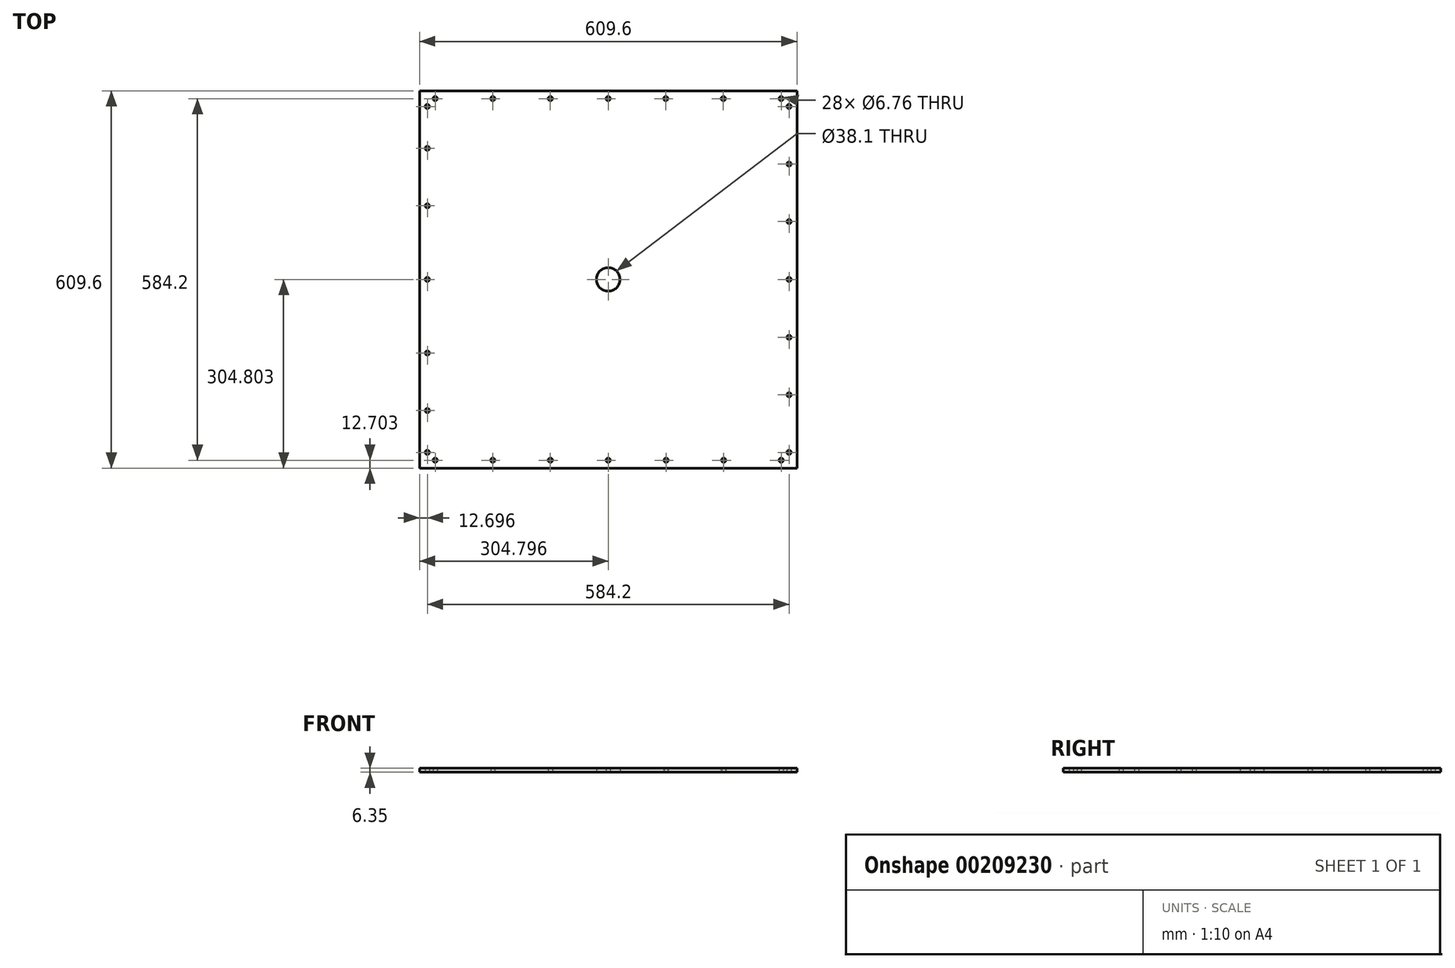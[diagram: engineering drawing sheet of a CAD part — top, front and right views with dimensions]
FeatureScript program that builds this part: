
annotation { "Feature Type Name" : "Feature", "Feature Type Description" : "" }
export const myFeature = defineFeature(function(context is Context, id is Id, definition is map)
    precondition{}
    {
        {
            var Q0;
            Q0=qCreatedBy(makeId("Top.planeOp"),FACE);
            var sketch = newSketch(context, id + "F0", { "sketchPlane" : qUnion([Q0])});
            skLineSegment(sketch, "E0.bottom", {"start": v(-439.06, 399.92) * mm, "end": v(170.54, 399.92) * mm});
            skLineSegment(sketch, "E0.top", {"start": v(-439.06, -209.68) * mm, "end": v(170.54, -209.68) * mm});
            skLineSegment(sketch, "E0.left", {"start": v(-439.06, 399.92) * mm, "end": v(-439.06, -209.68) * mm});
            skLineSegment(sketch, "E0.right", {"start": v(170.54, 399.92) * mm, "end": v(170.54, -209.68) * mm});
            skPoint(sketch, "E1", {"position": v(-439.06, 399.92) * mm});
            skPoint(sketch, "E2", {"position": v(170.54, 399.92) * mm});
            skPoint(sketch, "E3", {"position": v(170.54, -209.68) * mm});
            skPoint(sketch, "E4", {"position": v(-439.06, -209.68) * mm});
            skLineSegment(sketch, "E5", {"start": v(-439.06, 399.92) * mm, "end": v(170.54, -209.68) * mm, "construction": true});
            skLineSegment(sketch, "E6", {"start": v(170.54, 399.92) * mm, "end": v(-439.06, -209.68) * mm, "construction": true});
            skPoint(sketch, "E7", {"position": v(-134.26, 95.12) * mm});
            skCircle(sketch, "E8", {"center": v(-134.26, 95.12) * mm, "radius": 19.05 * mm});
            skPoint(sketch, "E9", {"position": v(-134.26, 399.92) * mm});
            skPoint(sketch, "E10", {"position": v(-426.36, 399.92) * mm});
            skPoint(sketch, "E11", {"position": v(157.84, 399.92) * mm});
            skPoint(sketch, "E12", {"position": v(170.54, 387.22) * mm});
            skPoint(sketch, "E13", {"position": v(-439.06, 387.22) * mm});
            skPoint(sketch, "E14", {"position": v(-439.06, -196.98) * mm});
            skPoint(sketch, "E15", {"position": v(-426.36, -209.68) * mm});
            skPoint(sketch, "E16", {"position": v(157.84, -209.68) * mm});
            skPoint(sketch, "E17", {"position": v(170.54, -196.98) * mm});
            skLineSegment(sketch, "E18", {"start": v(-439.06, 387.22) * mm, "end": v(170.54, 387.22) * mm, "construction": true});
            skLineSegment(sketch, "E19", {"start": v(-439.06, -196.98) * mm, "end": v(170.54, -196.98) * mm, "construction": true});
            skLineSegment(sketch, "E20", {"start": v(-439.06, -196.98) * mm, "end": v(-439.06, -106.24) * mm, "construction": true});
            skLineSegment(sketch, "E21", {"start": v(-426.36, 399.92) * mm, "end": v(-426.36, -209.68) * mm, "construction": true});
            skLineSegment(sketch, "E22", {"start": v(157.84, 399.92) * mm, "end": v(157.84, -209.68) * mm, "construction": true});
            skCircle(sketch, "E23", {"center": v(-134.26, 387.22) * mm, "radius": 3.18 * mm, "construction": true});
            skPoint(sketch, "E24", {"position": v(-413.66, 387.22) * mm});
            skPoint(sketch, "E25", {"position": v(145.14, 387.22) * mm});
            skPoint(sketch, "E26", {"position": v(-320.7, 387.22) * mm});
            skPoint(sketch, "E27", {"position": v(-227.74, 387.22) * mm});
            skPoint(sketch, "E28", {"position": v(-41.3, 387.22) * mm});
            skPoint(sketch, "E29", {"position": v(51.66, 387.22) * mm});
            skPoint(sketch, "E30", {"position": v(-426.36, 374.52) * mm});
            skPoint(sketch, "E31", {"position": v(-426.36, 95.12) * mm});
            skPoint(sketch, "E32", {"position": v(-426.36, -184.28) * mm});
            skPoint(sketch, "E33", {"position": v(-426.36, 306.96) * mm});
            skPoint(sketch, "E34", {"position": v(-426.36, -116.71) * mm});
            skPoint(sketch, "E35", {"position": v(-426.36, 214) * mm});
            skPoint(sketch, "E36", {"position": v(-426.36, -23.75) * mm});
            skPoint(sketch, "E37", {"position": v(-413.66, -196.98) * mm});
            skPoint(sketch, "E38", {"position": v(145.14, -196.98) * mm});
            skPoint(sketch, "E39", {"position": v(-134.26, -196.98) * mm});
            skPoint(sketch, "E40", {"position": v(-320.7, -196.98) * mm});
            skPoint(sketch, "E41", {"position": v(52.17, -196.98) * mm});
            skPoint(sketch, "E42", {"position": v(-227.74, -196.98) * mm});
            skPoint(sketch, "E43", {"position": v(-40.8, -196.98) * mm});
            skPoint(sketch, "E44", {"position": v(157.84, 374.52) * mm});
            skPoint(sketch, "E45", {"position": v(157.84, -184.28) * mm});
            skPoint(sketch, "E46", {"position": v(157.84, 95.12) * mm});
            skPoint(sketch, "E47", {"position": v(157.84, 281.56) * mm});
            skPoint(sketch, "E48", {"position": v(157.84, -91.31) * mm});
            skPoint(sketch, "E49", {"position": v(157.84, 1.65) * mm});
            skPoint(sketch, "E50", {"position": v(157.84, 188.6) * mm});
            skCircle(sketch, "E51", {"center": v(-413.66, 387.22) * mm, "radius": 3.18 * mm});
            skCircle(sketch, "E52", {"center": v(-320.7, 387.22) * mm, "radius": 3.18 * mm});
            skCircle(sketch, "E53", {"center": v(-227.74, 387.22) * mm, "radius": 3.18 * mm});
            skCircle(sketch, "E54", {"center": v(-426.36, 374.52) * mm, "radius": 3.18 * mm});
            skCircle(sketch, "E55", {"center": v(-426.36, 306.96) * mm, "radius": 3.18 * mm});
            skCircle(sketch, "E56", {"center": v(-426.36, 214) * mm, "radius": 3.18 * mm});
            skCircle(sketch, "E57", {"center": v(-426.36, 95.12) * mm, "radius": 3.18 * mm});
            skCircle(sketch, "E58", {"center": v(-426.36, -23.75) * mm, "radius": 3.18 * mm});
            skCircle(sketch, "E59", {"center": v(-426.36, -116.71) * mm, "radius": 3.18 * mm});
            skCircle(sketch, "E60", {"center": v(-426.36, -184.28) * mm, "radius": 3.18 * mm});
            skCircle(sketch, "E61", {"center": v(-413.66, -196.98) * mm, "radius": 3.18 * mm});
            skCircle(sketch, "E62", {"center": v(-320.7, -196.98) * mm, "radius": 3.18 * mm});
            skCircle(sketch, "E63", {"center": v(-227.74, -196.98) * mm, "radius": 3.18 * mm});
            skCircle(sketch, "E64", {"center": v(-134.26, -196.98) * mm, "radius": 3.18 * mm});
            skCircle(sketch, "E65", {"center": v(-40.8, -196.98) * mm, "radius": 3.18 * mm});
            skCircle(sketch, "E66", {"center": v(52.17, -196.98) * mm, "radius": 3.18 * mm});
            skCircle(sketch, "E67", {"center": v(145.14, -196.98) * mm, "radius": 3.18 * mm});
            skCircle(sketch, "E68", {"center": v(157.84, -184.28) * mm, "radius": 3.18 * mm});
            skCircle(sketch, "E69", {"center": v(157.84, -91.31) * mm, "radius": 3.18 * mm});
            skCircle(sketch, "E70", {"center": v(157.84, 1.65) * mm, "radius": 3.18 * mm});
            skCircle(sketch, "E71", {"center": v(157.84, 95.12) * mm, "radius": 3.18 * mm});
            skCircle(sketch, "E72", {"center": v(157.84, 188.6) * mm, "radius": 3.18 * mm});
            skCircle(sketch, "E73", {"center": v(157.84, 281.56) * mm, "radius": 3.18 * mm});
            skCircle(sketch, "E74", {"center": v(157.84, 374.52) * mm, "radius": 3.18 * mm});
            skCircle(sketch, "E75", {"center": v(145.14, 387.22) * mm, "radius": 3.18 * mm});
            skCircle(sketch, "E76", {"center": v(51.66, 387.22) * mm, "radius": 3.18 * mm});
            skCircle(sketch, "E77", {"center": v(-41.3, 387.22) * mm, "radius": 3.18 * mm});
            skSolve(sketch);
        }
        {
            var Q0;
            Q0=makeQuery(id+"F0.imprint","IMPRINT",FACE,{"disambiguationData":[TD([[makeQuery(id+"F0.imprint","IMPRINT",EDGE,{"derivedFrom":sQuery(id+"F0.wireOp",EDGE,"E0.bottom")}),-1.0]])]});
            var Q1;
            Q1=makeQuery(id+"F0.imprint","IMPRINT",FACE,{"disambiguationData":[TD([[makeQuery(id+"F0.imprint","IMPRINT",EDGE,{"derivedFrom":sQuery(id+"F0.wireOp",EDGE,"E65")}),1.0]])]});
            var Q2;
            Q2=makeQuery(id+"F0.imprint","IMPRINT",FACE,{"disambiguationData":[TD([[makeQuery(id+"F0.imprint","IMPRINT",EDGE,{"derivedFrom":sQuery(id+"F0.wireOp",EDGE,"E71")}),1.0]])]});
            var Q3;
            Q3=makeQuery(id+"F0.imprint","IMPRINT",FACE,{"disambiguationData":[TD([[makeQuery(id+"F0.imprint","IMPRINT",EDGE,{"derivedFrom":sQuery(id+"F0.wireOp",EDGE,"E75")}),1.0]])]});
            var Q4;
            Q4=makeQuery(id+"F0.imprint","IMPRINT",FACE,{"disambiguationData":[TD([[makeQuery(id+"F0.imprint","IMPRINT",EDGE,{"derivedFrom":sQuery(id+"F0.wireOp",EDGE,"E77")}),1.0]])]});
            var Q5;
            Q5=makeQuery(id+"F0.imprint","IMPRINT",FACE,{"disambiguationData":[TD([[makeQuery(id+"F0.imprint","IMPRINT",EDGE,{"derivedFrom":sQuery(id+"F0.wireOp",EDGE,"E73")}),1.0]])]});
            var Q6;
            Q6=makeQuery(id+"F0.imprint","IMPRINT",FACE,{"disambiguationData":[TD([[makeQuery(id+"F0.imprint","IMPRINT",EDGE,{"derivedFrom":sQuery(id+"F0.wireOp",EDGE,"E67")}),1.0]])]});
            var Q7;
            Q7=makeQuery(id+"F0.imprint","IMPRINT",FACE,{"disambiguationData":[TD([[makeQuery(id+"F0.imprint","IMPRINT",EDGE,{"derivedFrom":sQuery(id+"F0.wireOp",EDGE,"E70")}),1.0]])]});
            var Q8;
            Q8=makeQuery(id+"F0.imprint","IMPRINT",FACE,{"disambiguationData":[TD([[makeQuery(id+"F0.imprint","IMPRINT",EDGE,{"derivedFrom":sQuery(id+"F0.wireOp",EDGE,"E56")}),1.0]])]});
            var Q9;
            Q9=makeQuery(id+"F0.imprint","IMPRINT",FACE,{"disambiguationData":[TD([[makeQuery(id+"F0.imprint","IMPRINT",EDGE,{"derivedFrom":sQuery(id+"F0.wireOp",EDGE,"E64")}),1.0]])]});
            var Q10;
            Q10=makeQuery(id+"F0.imprint","IMPRINT",FACE,{"disambiguationData":[TD([[makeQuery(id+"F0.imprint","IMPRINT",EDGE,{"derivedFrom":sQuery(id+"F0.wireOp",EDGE,"E63")}),1.0]])]});
            var Q11;
            Q11=makeQuery(id+"F0.imprint","IMPRINT",FACE,{"disambiguationData":[TD([[makeQuery(id+"F0.imprint","IMPRINT",EDGE,{"derivedFrom":sQuery(id+"F0.wireOp",EDGE,"E66")}),1.0]])]});
            var Q12;
            Q12=makeQuery(id+"F0.imprint","IMPRINT",FACE,{"disambiguationData":[TD([[makeQuery(id+"F0.imprint","IMPRINT",EDGE,{"derivedFrom":sQuery(id+"F0.wireOp",EDGE,"E62")}),1.0]])]});
            var Q13;
            Q13=makeQuery(id+"F0.imprint","IMPRINT",FACE,{"disambiguationData":[TD([[makeQuery(id+"F0.imprint","IMPRINT",EDGE,{"derivedFrom":sQuery(id+"F0.wireOp",EDGE,"E60")}),1.0]])]});
            var Q14;
            Q14=makeQuery(id+"F0.imprint","IMPRINT",FACE,{"disambiguationData":[TD([[makeQuery(id+"F0.imprint","IMPRINT",EDGE,{"derivedFrom":sQuery(id+"F0.wireOp",EDGE,"E59")}),1.0]])]});
            var Q15;
            Q15=makeQuery(id+"F0.imprint","IMPRINT",FACE,{"disambiguationData":[TD([[makeQuery(id+"F0.imprint","IMPRINT",EDGE,{"derivedFrom":sQuery(id+"F0.wireOp",EDGE,"E61")}),1.0]])]});
            var Q16;
            Q16=makeQuery(id+"F0.imprint","IMPRINT",FACE,{"disambiguationData":[TD([[makeQuery(id+"F0.imprint","IMPRINT",EDGE,{"derivedFrom":sQuery(id+"F0.wireOp",EDGE,"E53")}),1.0]])]});
            var Q17;
            Q17=makeQuery(id+"F0.imprint","IMPRINT",FACE,{"disambiguationData":[TD([[makeQuery(id+"F0.imprint","IMPRINT",EDGE,{"derivedFrom":sQuery(id+"F0.wireOp",EDGE,"E58")}),1.0]])]});
            var Q18;
            Q18=makeQuery(id+"F0.imprint","IMPRINT",FACE,{"disambiguationData":[TD([[makeQuery(id+"F0.imprint","IMPRINT",EDGE,{"derivedFrom":sQuery(id+"F0.wireOp",EDGE,"E68")}),1.0]])]});
            var Q19;
            Q19=makeQuery(id+"F0.imprint","IMPRINT",FACE,{"disambiguationData":[TD([[makeQuery(id+"F0.imprint","IMPRINT",EDGE,{"derivedFrom":sQuery(id+"F0.wireOp",EDGE,"E57")}),1.0]])]});
            var Q20;
            Q20=makeQuery(id+"F0.imprint","IMPRINT",FACE,{"disambiguationData":[TD([[makeQuery(id+"F0.imprint","IMPRINT",EDGE,{"derivedFrom":sQuery(id+"F0.wireOp",EDGE,"E55")}),1.0]])]});
            var Q21;
            Q21=makeQuery(id+"F0.imprint","IMPRINT",FACE,{"disambiguationData":[TD([[makeQuery(id+"F0.imprint","IMPRINT",EDGE,{"derivedFrom":sQuery(id+"F0.wireOp",EDGE,"E74")}),1.0]])]});
            var Q22;
            Q22=makeQuery(id+"F0.imprint","IMPRINT",FACE,{"disambiguationData":[TD([[makeQuery(id+"F0.imprint","IMPRINT",EDGE,{"derivedFrom":sQuery(id+"F0.wireOp",EDGE,"E52")}),1.0]])]});
            var Q23;
            Q23=makeQuery(id+"F0.imprint","IMPRINT",FACE,{"disambiguationData":[TD([[makeQuery(id+"F0.imprint","IMPRINT",EDGE,{"derivedFrom":sQuery(id+"F0.wireOp",EDGE,"E51")}),1.0]])]});
            var Q24;
            Q24=makeQuery(id+"F0.imprint","IMPRINT",FACE,{"disambiguationData":[TD([[makeQuery(id+"F0.imprint","IMPRINT",EDGE,{"derivedFrom":sQuery(id+"F0.wireOp",EDGE,"E72")}),1.0]])]});
            var Q25;
            Q25=makeQuery(id+"F0.imprint","IMPRINT",FACE,{"disambiguationData":[TD([[makeQuery(id+"F0.imprint","IMPRINT",EDGE,{"derivedFrom":sQuery(id+"F0.wireOp",EDGE,"E76")}),1.0]])]});
            var Q26;
            Q26=makeQuery(id+"F0.imprint","IMPRINT",FACE,{"disambiguationData":[TD([[makeQuery(id+"F0.imprint","IMPRINT",EDGE,{"derivedFrom":sQuery(id+"F0.wireOp",EDGE,"E69")}),1.0]])]});
            var Q27;
            Q27=makeQuery(id+"F0.imprint","IMPRINT",FACE,{"disambiguationData":[TD([[makeQuery(id+"F0.imprint","IMPRINT",EDGE,{"derivedFrom":sQuery(id+"F0.wireOp",EDGE,"E54")}),1.0]])]});
            extrude(context, id + "F1", {"entities" : qUnion([Q0, Q1, Q2, Q3, Q4, Q5, Q6, Q7, Q8, Q9, Q10, Q11, Q12, Q13, Q14, Q15, Q16, Q17, Q18, Q19, Q20, Q21, Q22, Q23, Q24, Q25, Q26, Q27]), "depth" : 6.35 * mm});
        }
        {
            var Q0;
            Q0=sQuery(id+"F0.wireOp",VERTEX,"E52.center");
            var Q1;
            Q1=sQuery(id+"F0.wireOp",VERTEX,"E24");
            var Q2;
            Q2=sQuery(id+"F0.wireOp",VERTEX,"E30");
            var Q3;
            Q3=sQuery(id+"F0.wireOp",VERTEX,"E55.center");
            var Q4;
            Q4=sQuery(id+"F0.wireOp",VERTEX,"E35");
            var Q5;
            Q5=sQuery(id+"F0.wireOp",VERTEX,"E31");
            var Q6;
            Q6=sQuery(id+"F0.wireOp",VERTEX,"E58.center");
            var Q7;
            Q7=sQuery(id+"F0.wireOp",VERTEX,"E59.center");
            var Q8;
            Q8=sQuery(id+"F0.wireOp",VERTEX,"E32");
            var Q9;
            Q9=sQuery(id+"F0.wireOp",VERTEX,"E37");
            var Q10;
            Q10=sQuery(id+"F0.wireOp",VERTEX,"E62.center");
            var Q11;
            Q11=sQuery(id+"F0.wireOp",VERTEX,"E63.center");
            var Q12;
            Q12=sQuery(id+"F0.wireOp",VERTEX,"E64.center");
            var Q13;
            Q13=sQuery(id+"F0.wireOp",VERTEX,"E65.center");
            var Q14;
            Q14=sQuery(id+"F0.wireOp",VERTEX,"E41");
            var Q15;
            Q15=sQuery(id+"F0.wireOp",VERTEX,"E38");
            var Q16;
            Q16=sQuery(id+"F0.wireOp",VERTEX,"E68.center");
            var Q17;
            Q17=sQuery(id+"F0.wireOp",VERTEX,"E48");
            var Q18;
            Q18=sQuery(id+"F0.wireOp",VERTEX,"E49");
            var Q19;
            Q19=sQuery(id+"F0.wireOp",VERTEX,"E71.center");
            var Q20;
            Q20=sQuery(id+"F0.wireOp",VERTEX,"E72.center");
            var Q21;
            Q21=sQuery(id+"F0.wireOp",VERTEX,"E73.center");
            var Q22;
            Q22=sQuery(id+"F0.wireOp",VERTEX,"E44");
            var Q23;
            Q23=sQuery(id+"F0.wireOp",VERTEX,"E75.center");
            var Q24;
            Q24=sQuery(id+"F0.wireOp",VERTEX,"E29");
            var Q25;
            Q25=sQuery(id+"F0.wireOp",VERTEX,"E28");
            var Q26;
            Q26=sQuery(id+"F0.wireOp",VERTEX,"E23.center");
            var Q27;
            Q27=sQuery(id+"F0.wireOp",VERTEX,"E27");
            var Q28;
            Q28=makeQuery(id+"F1.opExtrude","SWEPT_BODY",BODY,{"disambiguationData":[OSD([sQuery(id+"F0.wireOp",EDGE,"E0.bottom"),sQuery(id+"F0.wireOp",EDGE,"E0.top"),sQuery(id+"F0.wireOp",EDGE,"E0.left"),sQuery(id+"F0.wireOp",EDGE,"E0.right")])]});
            hole(context, id + "F2", {"style" : HoleStyle.SIMPLE, "endStyle" : HoleEndStyle.BLIND, "oppositeDirection" : true, "standardTappedOrClearance" : lookupTablePath({ "standard" : "ANSI", "fit" : "Normal (ASME)", "size" : "1/4", "type" : "Clearance" }), "standardBlindInLast" : lookupTablePath({ "fit" : "Free", "standard" : "ANSI", "size" : "1/4", "type" : "Clearance" }), "holeDiameter" : 6.76 * mm, "holeDepth" : 6.35 * mm, "locations" : qUnion([Q0, Q1, Q2, Q3, Q4, Q5, Q6, Q7, Q8, Q9, Q10, Q11, Q12, Q13, Q14, Q15, Q16, Q17, Q18, Q19, Q20, Q21, Q22, Q23, Q24, Q25, Q26, Q27]), "scope" : qUnion([Q28])});
        }
    });
